# Revit family: Lighting-Wall_Mount-Lutron_Ivalo-Aliante_Demi_Sconce
name_source: partatom
category: Lighting Fixtures
revit_build: Autodesk Revit 2015 (Build: 20140905_0730(x64)
units: mm (PartAtom-declared; Revit-internal decimal feet)

## types (4) — shared parameters
120 Volts = Yes
277 Volts = No
ADA Compliant = Yes
Assembly Code = D5020200
Brand = Ivalo Lighting
Color Filter = 16777215
Default Elevation = 6' - 0"
Dimming Lamp Color Temperature Shift = <None>
Lamp = 42W Compact Fluorescent
Lamp Quantity = 1
Load Classification = Lighting
Lumens Per Lamp = 3200 lm
Manufacturer = Lutron Electronics
Mounting = Wall Mounted
Number of Poles = 1
Overall Depth = 0' - 4"
Product Page URL = http://www.ivalolighting.com
Product data url = https://bimobject.com
Series = Aliante
Tilt Angle = 0.00°
Total Lumens = 3200 lm
URL = http://www.lutron.com
Version = 2
Voltage = 120 V

## per-type parameters (varying)
| type | Apparent Load | Description | Direct and Indirect Distribution | Fixture Shell Material | Indirect Distribution | Model | Overall Height | Overall Width | Photometric Web File | Rear Frame Height | Revolve Back Offset | Slot Void Front Offset | Top Void Offset | Unit Weight | Wattage Comments |
| 21 inch Interior Direct/Indirect | 47 VA | Interior Direct/Indirect Decorative Demi-Sconce | Yes | Aluminum - Lutron Ivalo - Anodized Clear | No | AND211422W | 1' - 9" | 0' - 6 3/32" | Aliante 21in Interior Demi Sconce Fluorescent IES Data.ies | 1' - 3 1/2" | 0' - 0 9/32" | 0' - 0" | 0' - 0 11/32" | 4.50 lb | 47W |
| 21 inch Interior Indirect | 47 VA | Interior Indirect Decorative Demi-Sconce | No | Aluminum - Lutron Ivalo - Anodized Clear | Yes | ANN211422W | 1' - 9" | 0' - 6 3/32" | Aliante 21in Interior Demi Sconce Fluorescent IES Data.ies | 1' - 3 1/2" | 0' - 0 9/32" | 0' - 2" | 0' - 0 11/32" | 4.50 lb | 47W |
| 27 inch Interior Indirect | 50 VA | Interior Indirect Decorative Demi-Sconce | No | Aluminum - Lutron Ivalo - Anodized Clear | Yes | ANN271422W | 2' - 3" | 0' - 6 1/2" | Aliante 27in Interior Demi Sconce Fluorescent IES Data.ies | 1' - 10" | 0' - 0 3/8" | 0' - 2" | 0' - 0 5/16" | 5.00 lb | 49.8W |
| 27 inch Exterior Indirect | 47 VA | Exterior Indirect Decorative Demi-Sconce | No | Aluminum - Lutron Ivalo - Silver - Powder Coat | Yes | AEN271422W | 2' - 3" | 0' - 6 1/2" | Aliante 27in Exterior Demi Sconce Fluorescent IES Data.ies | 1' - 10" | 0' - 0 3/8" | 0' - 2" | 0' - 0 5/16" | 6.80 lb | 46.6W |

## geometry (parser evidence)
native form markers: Blend x8, Revolve x1, Sweep x3
no freeform markers — native parametric forms only
